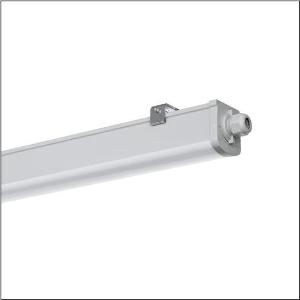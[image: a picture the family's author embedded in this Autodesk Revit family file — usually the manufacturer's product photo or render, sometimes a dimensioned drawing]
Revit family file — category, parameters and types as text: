
# Revit family: monsun_r__31_51fa20dp430b_5f21
name_source: partatom
category: Lighting Fixtures
units: mm (PartAtom-declared; Revit-internal decimal feet)

## family parameters
Cut with Voids When Loaded = No
Host = Face
Light Source = No
Part Type = Normal
Room Calculation Point = No
Round Connector Dimension = Use Diameter
Shared = No

## types (1)
- Monsun® 31 (1 x LED, 3800 lm, 28 W, 4000K)
    Apparent Load = 28 VA
    CIE Flux Codes = 42 72 91 92 100
    Color Rendering = 80
    Color Temperature = 4000K
    Default Elevation = 1800 mm
    Description = Monsun® 31, damp-proof luminaire, primary optical cover: diffuser, of PC, frosted, light emission: direct distribution, primary light characteristic: symmetric, installation type: surface-mounted, LED, rated luminous flux: 3.800lm, luminous efficacy: 136lm/W, light colour: 840, colour temperature: 4000K, control gear: ECG, with terminal, 5+1-pole, max. 2.5mm², through-wiring: 3x 2.5mm² + 3x 1.5mm², mains connection: 220..240V, AC, 50/60Hz, rated input power: 28W, housing, luminaire housing, of PC, light grey (RAL 7035), length: 1.458mm, width: 68mm, height: 76mm, protection rating (complete): IP66, insulation class (complete): insulation class II (safety insulation), certification: CE, ENEC, UKCA, protection symbol: D, impact resistance: IK08, permissible operating ambient temperature: -20..+40°C, corresponds to IFS (International Featured Standards) requirements for safety and quality in the food industry, contact your sales advisor before using the luminaires in applications with unclear chemical exposure, large temperature fluctuations or condensation-forming humidity, packaging unit: 1 piece
    Height = 77 mm
    Lamp = 1 x LED
    Lamp Light Flux = 3800 lm
    Lamp Power = 28 W
    Lamp count = 1
    Length = 1518 mm
    Luminous efficacy = 136 lm/W
    Manufacturer = Siteco
    ModVariant = No
    Model = 51FA20DP430B
    Mounting Place = Ceiling
    Mounting Type = Surface mounted
    Number of Poles = 1
    OnlyDefault = Yes
    Power Factor = 1
    Product Name = Monsun® 31
    Product group = damp-proof luminaire
    ProductGroupID = 300
    Protection Class = Protection class II
    Protection Degree = IP 66
    RLX_Detail_Level = 1
    RLX_Emergency_Light_Flux = 0 lm
    RLX_Emergency_Type = 0
    RLX_Emergency_Type_DB = No
    RlxData = <blob elided: 33181 chars, md5=57fc108d>
    Socket = socket
    Standby Power = 0 W
    System Light Flux = 3800 lm
    System Power = 28 W
    Type Comments = Product without accessories
    Type Image = l_1006174.jpg
    URL = http://relux.com
    VarID = ---
    Voltage = 0 V
    Weight = 0.00 kg
    Width = 69 mm

## geometry (parser evidence)
native form markers: Blend x4, Sweep x11
no freeform markers — native parametric forms only
